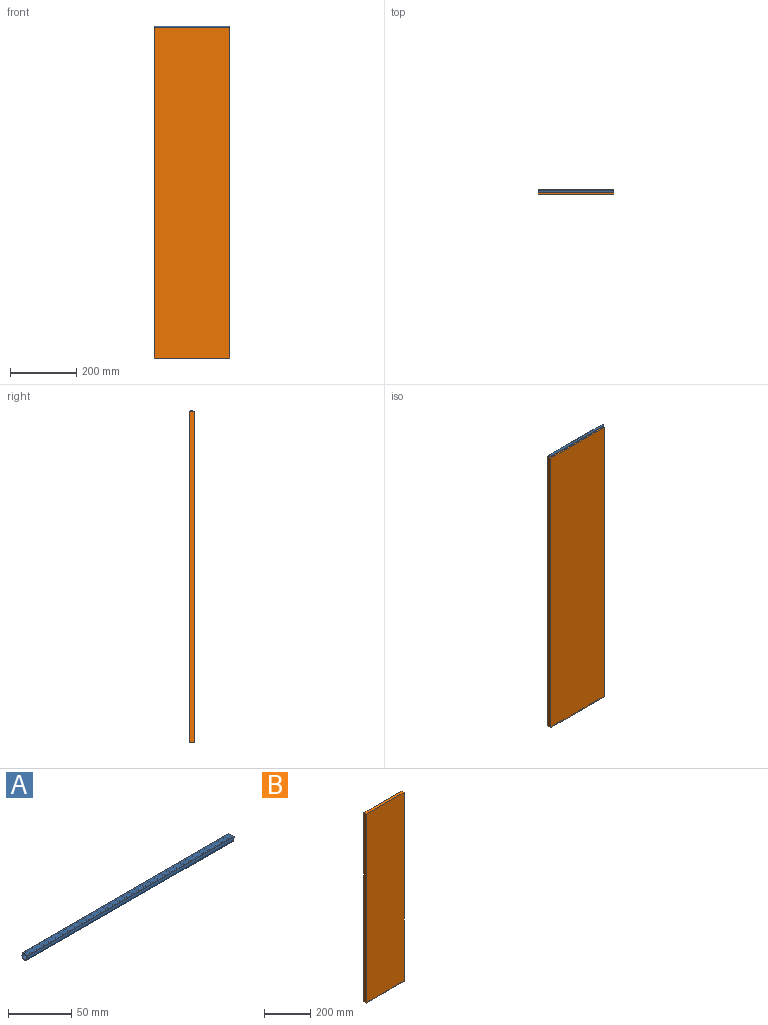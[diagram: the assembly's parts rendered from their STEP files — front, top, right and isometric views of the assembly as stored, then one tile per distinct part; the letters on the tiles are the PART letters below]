
ASSEMBLY  parts=2 mates=1
PART A: 10 faces, bbox 230x6.2x5.8 mm
  f0: plane 230x6mm, normal (0,0,1), area 1380mm2, adj f1,f7,f8,f9
  f1: plane 230x0.5mm, normal (0,-1,0), area 115mm2, adj f0,f2,f8,f9
  f2: plane 230x1.2mm, normal (0,0,-1), area 275.7mm2, adj f1,f3,f8,f9
  f3: cylinder r=3mm len=230mm, axis (1,0,0), area 3349.7mm2, adj f2,f4,f8,f9
  f4: plane 230x0.87mm, normal (0,0,-1), area 200.3mm2, adj f3,f7,f8,f9
  f5: cylinder r=2.5mm len=230mm, axis (1,0,0), area 3112.1mm2, adj f6,f8,f9
  f6: plane 230x2.11mm, normal (0,0,-1), area 485.1mm2, adj f5,f8,f9
  f7: plane 230x0.5mm, normal (0,1,0), area 115mm2, adj f0,f4,f8,f9
  f8: plane 6.16x5.77mm, normal (-1,0,0), area 10mm2, adj f0,f1,f2,f3,f4,f5,f6,f7
  f9: plane 6.16x5.77mm, normal (1,0,0), area 10mm2, adj f0,f1,f2,f3,f4,f5,f6,f7
PART B: 36 faces, bbox 230x15x1000 mm
  f0: plane 230x15mm, normal (0,0,1), area 3450mm2, adj f1,f3,f4,f5
  f1: plane 1000x15mm, normal (-1,0,0), area 15000mm2, adj f0,f2,f3,f4
  f2: plane 230x15mm, normal (0,0,-1), area 1338mm2, adj f1,f3,f4,f5,f6,f7,f8,f10
  f3: plane 1000x230mm, normal (0,-1,0), area 230000mm2, adj f0,f1,f2,f5
  f4: plane 1000x230mm, normal (0,1,0), area 229554.5mm2, adj f0,f1,f2,f5,f9,f13,f17,f30
  f5: plane 1000x15mm, normal (1,0,0), area 15000mm2, adj f0,f2,f3,f4
  f6: plane 12x2.75mm, normal (-1,0,0), area 33mm2, adj f2,f8,f9,f34
  f7: plane 12x2.75mm, normal (1,0,0), area 33mm2, adj f2,f8,f9,f35
  f8: plane 50x2.75mm, normal (0,1,0), area 137.5mm2, adj f2,f6,f7,f9
  f9: plane 54x14mm, normal (0,0,-1), area 697.7mm2, adj f4,f6,f7,f8,f27,f29,f34,f35
  f10: plane 12x2.75mm, normal (-1,0,0), area 33mm2, adj f2,f12,f13,f32
  f11: plane 12x2.75mm, normal (1,0,0), area 33mm2, adj f2,f12,f13,f33
  f12: plane 50x2.75mm, normal (0,1,0), area 137.5mm2, adj f2,f10,f11,f13
  f13: plane 54x14mm, normal (0,0,-1), area 697.7mm2, adj f4,f10,f11,f12,f23,f25,f32,f33
  f14: plane 12x2.75mm, normal (-1,0,0), area 33mm2, adj f2,f16,f17,f30
  f15: plane 12x2.75mm, normal (1,0,0), area 33mm2, adj f2,f16,f17,f31
  f16: plane 50x2.75mm, normal (0,1,0), area 137.5mm2, adj f2,f14,f15,f17
  f17: plane 54x14mm, normal (0,0,-1), area 697.7mm2, adj f4,f14,f15,f16,f19,f21,f30,f31
  f18: cone r=0mm half-angle=59deg, axis (0,0,-1), area 3.7mm2, adj f19
  f19: cylinder r=1mm len=12.25mm, axis (0,0,-1), area 77mm2, adj f17,f18
  f20: cone r=0mm half-angle=59deg, axis (0,0,-1), area 3.7mm2, adj f21
  f21: cylinder r=1mm len=12.25mm, axis (0,0,-1), area 77mm2, adj f17,f20
  f22: cone r=0mm half-angle=59deg, axis (0,0,-1), area 3.7mm2, adj f23
  f23: cylinder r=1mm len=12.25mm, axis (0,0,-1), area 77mm2, adj f13,f22
  f24: cone r=0mm half-angle=59deg, axis (0,0,-1), area 3.7mm2, adj f25
  f25: cylinder r=1mm len=12.25mm, axis (0,0,-1), area 77mm2, adj f13,f24
  f26: cone r=0mm half-angle=59deg, axis (0,0,-1), area 3.7mm2, adj f27
  f27: cylinder r=1mm len=12.25mm, axis (0,0,-1), area 77mm2, adj f9,f26
  f28: cone r=0mm half-angle=59deg, axis (0,0,-1), area 3.7mm2, adj f29
  f29: cylinder r=1mm len=12.25mm, axis (0,0,-1), area 77mm2, adj f9,f28
  f30: plane 2.75x2mm, normal (-0.71,0.71,0), area 7.8mm2, adj f2,f4,f14,f17
  f31: plane 2.75x2mm, normal (0.71,0.71,0), area 7.8mm2, adj f2,f4,f15,f17
  f32: plane 2.75x2mm, normal (-0.71,0.71,0), area 7.8mm2, adj f2,f4,f10,f13
  f33: plane 2.75x2mm, normal (0.71,0.71,0), area 7.8mm2, adj f2,f4,f11,f13
  f34: plane 2.75x2mm, normal (-0.71,0.71,0), area 7.8mm2, adj f2,f4,f6,f9
  f35: plane 2.75x2mm, normal (0.71,0.71,0), area 7.8mm2, adj f2,f4,f7,f9
PLACE A rot(axis=(0,1,0),180deg) t=(0,0.16,180)mm
PLACE B at identity fixed
MATE fastened A.f0 <-> B.f0  axis (0,0,-1) through (0,7.5,1000)mm
